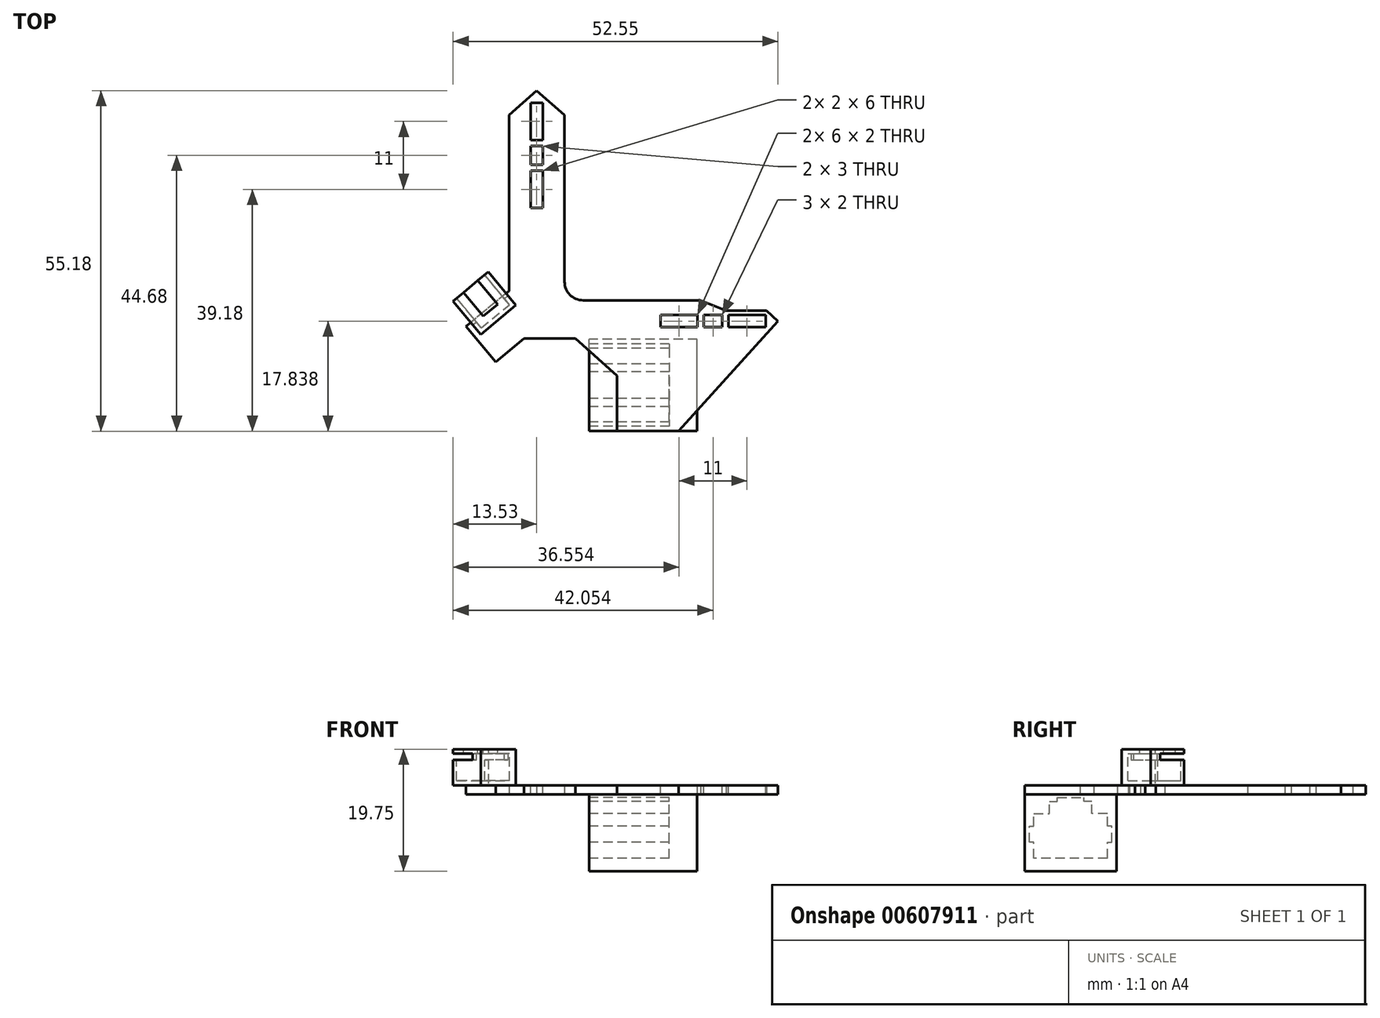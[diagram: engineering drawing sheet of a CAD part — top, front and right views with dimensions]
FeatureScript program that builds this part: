
annotation { "Feature Type Name" : "Feature", "Feature Type Description" : "" }
export const myFeature = defineFeature(function(context is Context, id is Id, definition is map)
    precondition{}
    {
        {
            var Q0;
            Q0=qCreatedBy(makeId("Top.planeOp"),FACE);
            var sketch = newSketch(context, id + "F0", { "sketchPlane" : qUnion([Q0])});
            skLineSegment(sketch, "E0", {"start": v(0, 0) * mm, "end": v(-4.5, -3.97) * mm});
            skLineSegment(sketch, "E1", {"start": v(-4.5, -3.97) * mm, "end": v(-4.5, -32.47) * mm});
            skLineSegment(sketch, "E2", {"start": v(-4.5, -32.47) * mm, "end": v(-11.44, -38.2) * mm});
            skLineSegment(sketch, "E3", {"start": v(-11.44, -38.2) * mm, "end": v(-6.66, -43.98) * mm});
            skLineSegment(sketch, "E4", {"start": v(-6.66, -43.98) * mm, "end": v(-2.03, -40.16) * mm});
            skLineSegment(sketch, "E5", {"start": v(-2.03, -40.16) * mm, "end": v(6.27, -40.16) * mm});
            skLineSegment(sketch, "E6", {"start": v(6.27, -40.16) * mm, "end": v(12.96, -46.18) * mm});
            skLineSegment(sketch, "E7", {"start": v(12.96, -46.18) * mm, "end": v(12.96, -55.18) * mm});
            skLineSegment(sketch, "E8", {"start": v(12.96, -55.18) * mm, "end": v(22.96, -55.18) * mm});
            skLineSegment(sketch, "E9", {"start": v(22.96, -55.18) * mm, "end": v(39.02, -37.34) * mm});
            skLineSegment(sketch, "E10", {"start": v(39.02, -37.34) * mm, "end": v(37.17, -35.67) * mm});
            skLineSegment(sketch, "E11", {"start": v(37.17, -35.67) * mm, "end": v(30.67, -35.67) * mm});
            skLineSegment(sketch, "E12", {"start": v(30.67, -35.67) * mm, "end": v(26.5, -33.97) * mm});
            skLineSegment(sketch, "E13", {"start": v(26.5, -33.97) * mm, "end": v(7.5, -33.97) * mm});
            skLineSegment(sketch, "E14", {"start": v(4.5, -30.97) * mm, "end": v(4.5, -3.97) * mm});
            skLineSegment(sketch, "E15", {"start": v(4.5, -3.97) * mm, "end": v(0, 0) * mm});
            skLineSegment(sketch, "E16", {"start": v(-4.5, -3.97) * mm, "end": v(4.5, -3.97) * mm});
            skPoint(sketch, "E17.visualSharp", {"position": v(4.5, -33.97) * mm});
            skArc(sketch, "E17.filletArc", {"start": v(4.5, -30.97) * mm, "mid": v(5.38, -33.09) * mm, "end": v(7.5, -33.97) * mm});
            skSolve(sketch);
        }
        {
            var Q0;
            Q0=makeQuery(id+"F0.imprint","IMPRINT",FACE,{"disambiguationData":[TD([[makeQuery(id+"F0.imprint","IMPRINT",EDGE,{"derivedFrom":sQuery(id+"F0.wireOp",EDGE,"E1")}),1.0]])]});
            var Q1;
            Q1=makeQuery(id+"F0.imprint","IMPRINT",FACE,{"disambiguationData":[TD([[makeQuery(id+"F0.imprint","IMPRINT",EDGE,{"derivedFrom":sQuery(id+"F0.wireOp",EDGE,"E0")}),1.0]])]});
            extrude(context, id + "F1", {"entities" : qUnion([Q0, Q1]), "depth" : 1.5 * mm, "offsetDistance" : 25 * mm});
        }
        {
            var Q0;
            Q0=makeQuery(id+"F1.opExtrude","CAP_FACE",FACE,{"disambiguationData":[OSD([sQuery(id+"F0.wireOp",EDGE,"E0"),sQuery(id+"F0.wireOp",EDGE,"E1"),sQuery(id+"F0.wireOp",EDGE,"E2"),sQuery(id+"F0.wireOp",EDGE,"E3"),sQuery(id+"F0.wireOp",EDGE,"E4"),sQuery(id+"F0.wireOp",EDGE,"E5"),sQuery(id+"F0.wireOp",EDGE,"E6"),sQuery(id+"F0.wireOp",EDGE,"E7"),sQuery(id+"F0.wireOp",EDGE,"E8"),sQuery(id+"F0.wireOp",EDGE,"E9"),sQuery(id+"F0.wireOp",EDGE,"E10"),sQuery(id+"F0.wireOp",EDGE,"E11"),sQuery(id+"F0.wireOp",EDGE,"E12"),sQuery(id+"F0.wireOp",EDGE,"E13"),sQuery(id+"F0.wireOp",EDGE,"E14"),sQuery(id+"F0.wireOp",EDGE,"E15")])],"isStart":false});
            var sketch = newSketch(context, id + "F2", { "sketchPlane" : qUnion([Q0])});
            skLineSegment(sketch, "E18", {"start": v(0, 0) * mm, "end": v(0, -33.97) * mm});
            skLineSegment(sketch, "E19.bottom", {"start": v(-1, -2) * mm, "end": v(1, -2) * mm});
            skLineSegment(sketch, "E19.top", {"start": v(-1, -8) * mm, "end": v(1, -8) * mm});
            skLineSegment(sketch, "E19.left", {"start": v(-1, -2) * mm, "end": v(-1, -8) * mm});
            skLineSegment(sketch, "E19.right", {"start": v(1, -2) * mm, "end": v(1, -8) * mm});
            skLineSegment(sketch, "E20", {"start": v(0, -2) * mm, "end": v(0, -8) * mm});
            skLineSegment(sketch, "E21.bottom", {"start": v(-1, -9) * mm, "end": v(1, -9) * mm});
            skLineSegment(sketch, "E21.top", {"start": v(-1, -12) * mm, "end": v(1, -12) * mm});
            skLineSegment(sketch, "E21.left", {"start": v(-1, -9) * mm, "end": v(-1, -12) * mm});
            skLineSegment(sketch, "E21.right", {"start": v(1, -9) * mm, "end": v(1, -12) * mm});
            skLineSegment(sketch, "E22.bottom", {"start": v(-1, -13) * mm, "end": v(1, -13) * mm});
            skLineSegment(sketch, "E22.top", {"start": v(-1, -19) * mm, "end": v(1, -19) * mm});
            skLineSegment(sketch, "E22.left", {"start": v(-1, -13) * mm, "end": v(-1, -19) * mm});
            skLineSegment(sketch, "E22.right", {"start": v(1, -13) * mm, "end": v(1, -19) * mm});
            skLineSegment(sketch, "E23", {"start": v(39.02, -37.34) * mm, "end": v(4.5, -37.34) * mm});
            skLineSegment(sketch, "E24.bottom", {"start": v(31.02, -36.34) * mm, "end": v(37.02, -36.34) * mm});
            skLineSegment(sketch, "E24.top", {"start": v(31.02, -38.34) * mm, "end": v(37.02, -38.34) * mm});
            skLineSegment(sketch, "E24.left", {"start": v(31.02, -36.34) * mm, "end": v(31.02, -38.34) * mm});
            skLineSegment(sketch, "E24.right", {"start": v(37.02, -36.34) * mm, "end": v(37.02, -38.34) * mm});
            skLineSegment(sketch, "E25.bottom", {"start": v(27.02, -36.34) * mm, "end": v(30.02, -36.34) * mm});
            skLineSegment(sketch, "E25.top", {"start": v(27.02, -38.34) * mm, "end": v(30.02, -38.34) * mm});
            skLineSegment(sketch, "E25.left", {"start": v(27.02, -36.34) * mm, "end": v(27.02, -38.34) * mm});
            skLineSegment(sketch, "E25.right", {"start": v(30.02, -36.34) * mm, "end": v(30.02, -38.34) * mm});
            skLineSegment(sketch, "E26.bottom", {"start": v(20.02, -36.34) * mm, "end": v(26.02, -36.34) * mm});
            skLineSegment(sketch, "E26.top", {"start": v(20.02, -38.34) * mm, "end": v(26.02, -38.34) * mm});
            skLineSegment(sketch, "E26.left", {"start": v(20.02, -36.34) * mm, "end": v(20.02, -38.34) * mm});
            skLineSegment(sketch, "E26.right", {"start": v(26.02, -36.34) * mm, "end": v(26.02, -38.34) * mm});
            skLineSegment(sketch, "E27", {"start": v(37.02, -37.34) * mm, "end": v(31.02, -37.34) * mm});
            skLineSegment(sketch, "E28", {"start": v(27.02, -36.34) * mm, "end": v(30.02, -38.34) * mm});
            skPoint(sketch, "E29", {"position": v(28.52, -37.34) * mm});
            skLineSegment(sketch, "E30", {"start": v(-1, -9) * mm, "end": v(1, -12) * mm});
            skPoint(sketch, "E31", {"position": v(0, -10.5) * mm});
            skSolve(sketch);
        }
        {
            var Q0;
            {var subQ0=sQuery(id+"F2.wireOp",EDGE,"E19.left");Q0=makeQuery(id+"F2.imprint","IMPRINT",FACE,{"disambiguationData":[TD([[makeQuery(id+"F2.imprint","IMPRINT",EDGE,{"derivedFrom":subQ0}),1.0]])]});}
            var Q1;
            {var subQ0=sQuery(id+"F2.wireOp",EDGE,"E19.right");Q1=makeQuery(id+"F2.imprint","IMPRINT",FACE,{"disambiguationData":[TD([[makeQuery(id+"F2.imprint","IMPRINT",EDGE,{"derivedFrom":subQ0}),-1.0]])]});}
            var Q2;
            {var subQ5=sQuery(id+"F2.wireOp",EDGE,"E21.left");Q2=makeQuery(id+"F2.imprint","IMPRINT",FACE,{"disambiguationData":[TD([[makeQuery(id+"F2.imprint","IMPRINT",EDGE,{"derivedFrom":subQ5}),1.0]])]});}
            var Q3;
            {var subQ5=sQuery(id+"F2.wireOp",EDGE,"E21.right");Q3=makeQuery(id+"F2.imprint","IMPRINT",FACE,{"disambiguationData":[TD([[makeQuery(id+"F2.imprint","IMPRINT",EDGE,{"derivedFrom":subQ5}),-1.0]])]});}
            var Q4;
            {var subQ5=sQuery(id+"F2.wireOp",EDGE,"E22.left");Q4=makeQuery(id+"F2.imprint","IMPRINT",FACE,{"disambiguationData":[TD([[makeQuery(id+"F2.imprint","IMPRINT",EDGE,{"derivedFrom":subQ5}),1.0]])]});}
            var Q5;
            {var subQ5=sQuery(id+"F2.wireOp",EDGE,"E22.right");Q5=makeQuery(id+"F2.imprint","IMPRINT",FACE,{"disambiguationData":[TD([[makeQuery(id+"F2.imprint","IMPRINT",EDGE,{"derivedFrom":subQ5}),-1.0]])]});}
            var Q6;
            {var subQ5=sQuery(id+"F2.wireOp",EDGE,"E26.bottom");Q6=makeQuery(id+"F2.imprint","IMPRINT",FACE,{"disambiguationData":[TD([[makeQuery(id+"F2.imprint","IMPRINT",EDGE,{"derivedFrom":subQ5}),-1.0]])]});}
            var Q7;
            {var subQ5=sQuery(id+"F2.wireOp",EDGE,"E26.top");Q7=makeQuery(id+"F2.imprint","IMPRINT",FACE,{"disambiguationData":[TD([[makeQuery(id+"F2.imprint","IMPRINT",EDGE,{"derivedFrom":subQ5}),1.0]])]});}
            var Q8;
            {var subQ5=sQuery(id+"F2.wireOp",EDGE,"E25.top");Q8=makeQuery(id+"F2.imprint","IMPRINT",FACE,{"disambiguationData":[TD([[makeQuery(id+"F2.imprint","IMPRINT",EDGE,{"derivedFrom":subQ5}),1.0]])]});}
            var Q9;
            {var subQ0=sQuery(id+"F2.wireOp",EDGE,"E24.bottom");Q9=makeQuery(id+"F2.imprint","IMPRINT",FACE,{"disambiguationData":[TD([[makeQuery(id+"F2.imprint","IMPRINT",EDGE,{"derivedFrom":subQ0}),-1.0]])]});}
            var Q10;
            {var subQ0=sQuery(id+"F2.wireOp",EDGE,"E24.top");Q10=makeQuery(id+"F2.imprint","IMPRINT",FACE,{"disambiguationData":[TD([[makeQuery(id+"F2.imprint","IMPRINT",EDGE,{"derivedFrom":subQ0}),1.0]])]});}
            var Q11;
            {var subQ0=sQuery(id+"F2.wireOp",EDGE,"E21.bottom");var subQ1=sQuery(id+"F2.wireOp",EDGE,"E18");var subQ2=makeQuery(id+"F2.imprint","INTERSECT",VERTEX,{"derivedFrom":[subQ1,subQ0]});Q11=makeQuery(id+"F2.imprint","IMPRINT",FACE,{"disambiguationData":[TD([[makeQuery(id+"F2.imprint","IMPRINT",EDGE,{"disambiguationData":[TD([[subQ2,-1.0]])],"derivedFrom":subQ1}),-1.0]])]});}
            var Q12;
            {var subQ0=sQuery(id+"F2.wireOp",EDGE,"E21.top");var subQ1=sQuery(id+"F2.wireOp",EDGE,"E18");var subQ2=makeQuery(id+"F2.imprint","INTERSECT",VERTEX,{"derivedFrom":[subQ1,subQ0]});Q12=makeQuery(id+"F2.imprint","IMPRINT",FACE,{"disambiguationData":[TD([[makeQuery(id+"F2.imprint","IMPRINT",EDGE,{"disambiguationData":[TD([[subQ2,1.0]])],"derivedFrom":subQ1}),1.0]])]});}
            var Q13;
            {var subQ0=sQuery(id+"F2.wireOp",EDGE,"E25.left");var subQ1=sQuery(id+"F2.wireOp",EDGE,"E23");var subQ2=makeQuery(id+"F2.imprint","INTERSECT",VERTEX,{"derivedFrom":[subQ1,subQ0]});Q13=makeQuery(id+"F2.imprint","IMPRINT",FACE,{"disambiguationData":[TD([[makeQuery(id+"F2.imprint","IMPRINT",EDGE,{"disambiguationData":[TD([[subQ2,1.0]])],"derivedFrom":subQ1}),-1.0]])]});}
            var Q14;
            {var subQ5=sQuery(id+"F2.wireOp",EDGE,"E25.bottom");Q14=makeQuery(id+"F2.imprint","IMPRINT",FACE,{"disambiguationData":[TD([[makeQuery(id+"F2.imprint","IMPRINT",EDGE,{"derivedFrom":subQ5}),-1.0]])]});}
            var Q15;
            {var subQ0=sQuery(id+"F2.wireOp",EDGE,"E25.right");var subQ1=sQuery(id+"F2.wireOp",EDGE,"E23");var subQ2=makeQuery(id+"F2.imprint","INTERSECT",VERTEX,{"derivedFrom":[subQ1,subQ0]});Q15=makeQuery(id+"F2.imprint","IMPRINT",FACE,{"disambiguationData":[TD([[makeQuery(id+"F2.imprint","IMPRINT",EDGE,{"disambiguationData":[TD([[subQ2,-1.0]])],"derivedFrom":subQ1}),1.0]])]});}
            extrude(context, id + "F3", {"entities" : qUnion([Q0, Q1, Q2, Q3, Q4, Q5, Q6, Q7, Q8, Q9, Q10, Q11, Q12, Q13, Q14, Q15]), "operationType" : NewBodyOperationType.REMOVE, "endBound" : BoundingType.THROUGH_ALL, "oppositeDirection" : true, "depth" : 25 * mm, "offsetDistance" : 25 * mm});
        }
        {
            var Q0;
            Q0=makeQuery(id+"F1.opExtrude","CAP_FACE",FACE,{"disambiguationData":[OSD([sQuery(id+"F0.wireOp",EDGE,"E0"),sQuery(id+"F0.wireOp",EDGE,"E1"),sQuery(id+"F0.wireOp",EDGE,"E2"),sQuery(id+"F0.wireOp",EDGE,"E3"),sQuery(id+"F0.wireOp",EDGE,"E4"),sQuery(id+"F0.wireOp",EDGE,"E5"),sQuery(id+"F0.wireOp",EDGE,"E6"),sQuery(id+"F0.wireOp",EDGE,"E7"),sQuery(id+"F0.wireOp",EDGE,"E8"),sQuery(id+"F0.wireOp",EDGE,"E9"),sQuery(id+"F0.wireOp",EDGE,"E10"),sQuery(id+"F0.wireOp",EDGE,"E11"),sQuery(id+"F0.wireOp",EDGE,"E12"),sQuery(id+"F0.wireOp",EDGE,"E13"),sQuery(id+"F0.wireOp",EDGE,"E14"),sQuery(id+"F0.wireOp",EDGE,"E15")])],"isStart":false});
            var sketch = newSketch(context, id + "F4", { "sketchPlane" : qUnion([Q0])});
            skLineSegment(sketch, "E32.bottom", {"start": v(-13.53, -34.1) * mm, "end": v(-7.83, -29.38) * mm});
            skLineSegment(sketch, "E32.top", {"start": v(-9.07, -39.5) * mm, "end": v(-3.37, -34.78) * mm});
            skLineSegment(sketch, "E32.left", {"start": v(-13.53, -34.1) * mm, "end": v(-9.07, -39.5) * mm});
            skLineSegment(sketch, "E32.right", {"start": v(-7.83, -29.38) * mm, "end": v(-3.37, -34.78) * mm});
            skLineSegment(sketch, "E33.0", {"start": v(-4.5, -32.47) * mm, "end": v(-11.44, -38.2) * mm});
            skPoint(sketch, "E34", {"position": v(-10.66, -37.57) * mm});
            skSolve(sketch);
        }
        {
            var Q0;
            {var subQ0=sQuery(id+"F4.wireOp",EDGE,"E32.bottom");Q0=makeQuery(id+"F4.imprint","IMPRINT",FACE,{"disambiguationData":[TD([[makeQuery(id+"F4.imprint","IMPRINT",EDGE,{"derivedFrom":subQ0}),-1.0]])]});}
            var Q1;
            {var subQ0=sQuery(id+"F4.wireOp",EDGE,"E32.top");Q1=makeQuery(id+"F4.imprint","IMPRINT",FACE,{"disambiguationData":[TD([[makeQuery(id+"F4.imprint","IMPRINT",EDGE,{"derivedFrom":subQ0}),1.0]])]});}
            extrude(context, id + "F5", {"entities" : qUnion([Q0, Q1]), "depth" : 5.85 * mm, "offsetDistance" : 25 * mm});
        }
        {
            var Q0;
            Q0=makeQuery(id+"F5.opExtrude","SWEPT_FACE",FACE,{"disambiguationData":[OSD([sQuery(id+"F4.wireOp",EDGE,"E32.bottom")])]});
            var sketch = newSketch(context, id + "F6", { "sketchPlane" : qUnion([Q0])});
            skLineSegment(sketch, "E35.bottom", {"start": v(31.41, 2.25) * mm, "end": v(25.51, 2.25) * mm});
            skLineSegment(sketch, "E35.top", {"start": v(31.41, 6.6) * mm, "end": v(25.51, 6.6) * mm});
            skLineSegment(sketch, "E35.left", {"start": v(31.41, 2.25) * mm, "end": v(31.41, 6.6) * mm});
            skLineSegment(sketch, "E35.right", {"start": v(25.51, 2.25) * mm, "end": v(25.51, 6.6) * mm});
            skLineSegment(sketch, "E36.bottom", {"start": v(32.16, 6.6) * mm, "end": v(24.76, 6.6) * mm});
            skLineSegment(sketch, "E36.top", {"start": v(32.16, 5.6) * mm, "end": v(24.76, 5.6) * mm});
            skLineSegment(sketch, "E36.left", {"start": v(32.16, 6.6) * mm, "end": v(32.16, 5.6) * mm});
            skLineSegment(sketch, "E36.right", {"start": v(24.76, 6.6) * mm, "end": v(24.76, 5.6) * mm});
            skLineSegment(sketch, "E37.bottom", {"start": v(29.96, 6.6) * mm, "end": v(26.96, 6.6) * mm});
            skLineSegment(sketch, "E37.top", {"start": v(29.96, 7.35) * mm, "end": v(26.96, 7.35) * mm});
            skLineSegment(sketch, "E37.left", {"start": v(29.96, 6.6) * mm, "end": v(29.96, 7.35) * mm});
            skLineSegment(sketch, "E37.right", {"start": v(26.96, 6.6) * mm, "end": v(26.96, 7.35) * mm});
            skLineSegment(sketch, "E38", {"start": v(28.46, 7.35) * mm, "end": v(28.46, 2.25) * mm});
            skSolve(sketch);
        }
        {
            var Q0;
            {var subQ0=sQuery(id+"F6.wireOp",EDGE,"E35.left");var subQ1=sQuery(id+"F6.wireOp",EDGE,"E35.bottom");var subQ2=makeQuery(id+"F6.imprint","INTERSECT",VERTEX,{"derivedFrom":[subQ1,subQ0]});Q0=makeQuery(id+"F6.imprint","IMPRINT",FACE,{"disambiguationData":[TD([[makeQuery(id+"F6.imprint","IMPRINT",EDGE,{"disambiguationData":[TD([[subQ2,-1.0]])],"derivedFrom":subQ1}),-1.0]])]});}
            var Q1;
            {var subQ1=sQuery(id+"F6.wireOp",EDGE,"E36.bottom");var subQ6=sQuery(id+"F6.wireOp",EDGE,"E35.left");var subQ9=makeQuery(id+"F6.imprint","INTERSECT",VERTEX,{"derivedFrom":[subQ6,subQ1]});Q1=makeQuery(id+"F6.imprint","IMPRINT",FACE,{"disambiguationData":[TD([[makeQuery(id+"F6.imprint","IMPRINT",EDGE,{"disambiguationData":[TD([[subQ9,1.0]])],"derivedFrom":subQ6}),1.0]])]});}
            var Q2;
            {var subQ0=sQuery(id+"F6.wireOp",EDGE,"E35.right");var subQ1=sQuery(id+"F6.wireOp",EDGE,"E35.bottom");var subQ2=makeQuery(id+"F6.imprint","INTERSECT",VERTEX,{"derivedFrom":[subQ1,subQ0]});Q2=makeQuery(id+"F6.imprint","IMPRINT",FACE,{"disambiguationData":[TD([[makeQuery(id+"F6.imprint","IMPRINT",EDGE,{"disambiguationData":[TD([[subQ2,1.0]])],"derivedFrom":subQ1}),-1.0]])]});}
            var Q3;
            {var subQ1=sQuery(id+"F6.wireOp",EDGE,"E36.bottom");var subQ6=sQuery(id+"F6.wireOp",EDGE,"E35.right");var subQ9=makeQuery(id+"F6.imprint","INTERSECT",VERTEX,{"derivedFrom":[subQ6,subQ1]});Q3=makeQuery(id+"F6.imprint","IMPRINT",FACE,{"disambiguationData":[TD([[makeQuery(id+"F6.imprint","IMPRINT",EDGE,{"disambiguationData":[TD([[subQ9,1.0]])],"derivedFrom":subQ6}),-1.0]])]});}
            extrude(context, id + "F7", {"entities" : qUnion([Q0, Q1, Q2, Q3]), "operationType" : NewBodyOperationType.REMOVE, "oppositeDirection" : true, "depth" : (7 - 0.75) * mm, "offsetDistance" : 25 * mm});
        }
        {
            var Q0;
            {var subQ5=sQuery(id+"F6.wireOp",EDGE,"E36.left");Q0=makeQuery(id+"F6.imprint","IMPRINT",FACE,{"disambiguationData":[TD([[makeQuery(id+"F6.imprint","IMPRINT",EDGE,{"derivedFrom":subQ5}),-1.0]])]});}
            var Q1;
            {var subQ0=sQuery(id+"F6.wireOp",EDGE,"E37.left");Q1=makeQuery(id+"F6.imprint","IMPRINT",FACE,{"disambiguationData":[TD([[makeQuery(id+"F6.imprint","IMPRINT",EDGE,{"derivedFrom":subQ0}),1.0]])]});}
            var Q2;
            {var subQ0=sQuery(id+"F6.wireOp",EDGE,"E37.right");Q2=makeQuery(id+"F6.imprint","IMPRINT",FACE,{"disambiguationData":[TD([[makeQuery(id+"F6.imprint","IMPRINT",EDGE,{"derivedFrom":subQ0}),-1.0]])]});}
            var Q3;
            {var subQ5=sQuery(id+"F6.wireOp",EDGE,"E36.right");Q3=makeQuery(id+"F6.imprint","IMPRINT",FACE,{"disambiguationData":[TD([[makeQuery(id+"F6.imprint","IMPRINT",EDGE,{"derivedFrom":subQ5}),1.0]])]});}
            extrude(context, id + "F8", {"entities" : qUnion([Q0, Q1, Q2, Q3]), "operationType" : NewBodyOperationType.REMOVE, "oppositeDirection" : true, "depth" : (7 - 2) * mm, "offsetDistance" : 25 * mm});
        }
        {
            var Q0;
            Q0=makeQuery(id+"F1.opExtrude","CAP_FACE",FACE,{"disambiguationData":[OSD([sQuery(id+"F0.wireOp",EDGE,"E0"),sQuery(id+"F0.wireOp",EDGE,"E1"),sQuery(id+"F0.wireOp",EDGE,"E2"),sQuery(id+"F0.wireOp",EDGE,"E3"),sQuery(id+"F0.wireOp",EDGE,"E4"),sQuery(id+"F0.wireOp",EDGE,"E5"),sQuery(id+"F0.wireOp",EDGE,"E6"),sQuery(id+"F0.wireOp",EDGE,"E7"),sQuery(id+"F0.wireOp",EDGE,"E8"),sQuery(id+"F0.wireOp",EDGE,"E9"),sQuery(id+"F0.wireOp",EDGE,"E10"),sQuery(id+"F0.wireOp",EDGE,"E11"),sQuery(id+"F0.wireOp",EDGE,"E12"),sQuery(id+"F0.wireOp",EDGE,"E13"),sQuery(id+"F0.wireOp",EDGE,"E14"),sQuery(id+"F0.wireOp",EDGE,"E15"),sQuery(id+"F0.wireOp",EDGE,"E17.filletArc")])],"isStart":true});
            var sketch = newSketch(context, id + "F9", { "sketchPlane" : qUnion([Q0])});
            skLineSegment(sketch, "E39.bottom", {"start": v(25.96, 55.18) * mm, "end": v(8.46, 55.18) * mm});
            skLineSegment(sketch, "E39.top", {"start": v(25.96, 40.28) * mm, "end": v(8.46, 40.28) * mm});
            skLineSegment(sketch, "E39.left", {"start": v(25.96, 55.18) * mm, "end": v(25.96, 40.28) * mm});
            skLineSegment(sketch, "E39.right", {"start": v(8.46, 55.18) * mm, "end": v(8.46, 40.28) * mm});
            skLineSegment(sketch, "E40.0", {"start": v(22.96, 55.18) * mm, "end": v(39.02, 37.34) * mm});
            skSolve(sketch);
        }
        {
            var Q0;
            {var subQ1=makeQuery(id+"F1.opExtrude","CAP_EDGE",EDGE,{"disambiguationData":[OSD([sQuery(id+"F0.wireOp",EDGE,"E7")])],"isStart":true});Q0=makeQuery(id+"F9.imprint","IMPRINT",FACE,{"disambiguationData":[TD([[makeQuery(id+"F9.imprint","IMPRINT",EDGE,{"derivedFrom":subQ1}),1.0]])]});}
            var Q1;
            {var subQ1=sQuery(id+"F9.wireOp",EDGE,"E39.top");Q1=makeQuery(id+"F9.imprint","IMPRINT",FACE,{"disambiguationData":[TD([[makeQuery(id+"F9.imprint","IMPRINT",EDGE,{"derivedFrom":subQ1}),-1.0]])]});}
            var Q2;
            {var subQ0=sQuery(id+"F9.wireOp",EDGE,"E39.bottom");var subQ1=makeQuery(id+"F1.opExtrude","CAP_EDGE",EDGE,{"disambiguationData":[OSD([sQuery(id+"F0.wireOp",EDGE,"E9")])],"isStart":true});var subQ2=makeQuery(id+"F9.imprint","INTERSECT",VERTEX,{"derivedFrom":[subQ1,subQ0]});var subQ3=sQuery(id+"F9.wireOp",EDGE,"E39.left");var subQ4=makeQuery(id+"F9.imprint","INTERSECT",VERTEX,{"derivedFrom":[subQ0,subQ3]});Q2=makeQuery(id+"F9.imprint","IMPRINT",FACE,{"disambiguationData":[TD([[makeQuery(id+"F9.imprint","IMPRINT",EDGE,{"disambiguationData":[TD([[subQ2,1.0],[subQ4,-1.0]])],"derivedFrom":subQ0}),1.0]])]});}
            extrude(context, id + "F10", {"entities" : qUnion([Q0, Q1, Q2]), "depth" : 12.4 * mm, "offsetDistance" : 25 * mm});
        }
        {
            var Q0;
            Q0=makeQuery(id+"F10.opExtrude","SWEPT_FACE",FACE,{"disambiguationData":[OSD([sQuery(id+"F9.wireOp",EDGE,"E39.right")])]});
            var sketch = newSketch(context, id + "F11", { "sketchPlane" : qUnion([Q0])});
            skLineSegment(sketch, "E41", {"start": v(47.73, -12.4) * mm, "end": v(47.73, 0) * mm});
            skLineSegment(sketch, "E42", {"start": v(47.73, -10.3) * mm, "end": v(41.78, -10.3) * mm});
            skLineSegment(sketch, "E43", {"start": v(41.78, -10.3) * mm, "end": v(41.78, -7.7) * mm});
            skLineSegment(sketch, "E44", {"start": v(41.78, -7.7) * mm, "end": v(41.08, -7.7) * mm});
            skLineSegment(sketch, "E45", {"start": v(41.08, -7.7) * mm, "end": v(41.08, -5.1) * mm});
            skLineSegment(sketch, "E46", {"start": v(41.08, -5.1) * mm, "end": v(41.78, -5.1) * mm});
            skLineSegment(sketch, "E47", {"start": v(41.78, -5.1) * mm, "end": v(41.78, -3.1) * mm});
            skLineSegment(sketch, "E48", {"start": v(41.78, -3.1) * mm, "end": v(44.28, -3.1) * mm});
            skLineSegment(sketch, "E49", {"start": v(44.28, -3.1) * mm, "end": v(44.28, -1.1) * mm});
            skLineSegment(sketch, "E50", {"start": v(44.28, -1.1) * mm, "end": v(45.58, -1.1) * mm});
            skLineSegment(sketch, "E51", {"start": v(45.58, -1.1) * mm, "end": v(45.58, -0.5) * mm});
            skLineSegment(sketch, "E52", {"start": v(45.58, -0.5) * mm, "end": v(47.73, -0.5) * mm});
            skLineSegment(sketch, "E53.MirrorCS", {"start": v(47.73, -10.3) * mm, "end": v(53.68, -10.3) * mm});
            skLineSegment(sketch, "E54.MirrorCS", {"start": v(53.68, -10.3) * mm, "end": v(53.68, -7.7) * mm});
            skLineSegment(sketch, "E55.MirrorCS", {"start": v(54.38, -7.7) * mm, "end": v(54.38, -5.1) * mm});
            skLineSegment(sketch, "E56.MirrorCS", {"start": v(53.68, -7.7) * mm, "end": v(54.38, -7.7) * mm});
            skLineSegment(sketch, "E57.MirrorCS", {"start": v(54.38, -5.1) * mm, "end": v(53.68, -5.1) * mm});
            skLineSegment(sketch, "E58.MirrorCS", {"start": v(53.68, -5.1) * mm, "end": v(53.68, -3.1) * mm});
            skLineSegment(sketch, "E59.MirrorCS", {"start": v(51.18, -3.1) * mm, "end": v(51.18, -1.1) * mm});
            skLineSegment(sketch, "E60.MirrorCS", {"start": v(53.68, -3.1) * mm, "end": v(51.18, -3.1) * mm});
            skLineSegment(sketch, "E61.MirrorCS", {"start": v(51.18, -1.1) * mm, "end": v(49.88, -1.1) * mm});
            skLineSegment(sketch, "E62.MirrorCS", {"start": v(49.88, -0.5) * mm, "end": v(47.73, -0.5) * mm});
            skLineSegment(sketch, "E63.MirrorCS", {"start": v(49.88, -1.1) * mm, "end": v(49.88, -0.5) * mm});
            skSolve(sketch);
        }
        {
            var Q0;
            {var subQ0=sQuery(id+"F11.wireOp",EDGE,"E53.MirrorCS");Q0=makeQuery(id+"F11.imprint","IMPRINT",FACE,{"disambiguationData":[TD([[makeQuery(id+"F11.imprint","IMPRINT",EDGE,{"derivedFrom":subQ0}),1.0]])]});}
            var Q1;
            {var subQ0=sQuery(id+"F11.wireOp",EDGE,"E42");Q1=makeQuery(id+"F11.imprint","IMPRINT",FACE,{"disambiguationData":[TD([[makeQuery(id+"F11.imprint","IMPRINT",EDGE,{"derivedFrom":subQ0}),-1.0]])]});}
            extrude(context, id + "F12", {"entities" : qUnion([Q0, Q1]), "operationType" : NewBodyOperationType.REMOVE, "oppositeDirection" : true, "depth" : 13 * mm, "offsetDistance" : 25 * mm});
        }
    });
